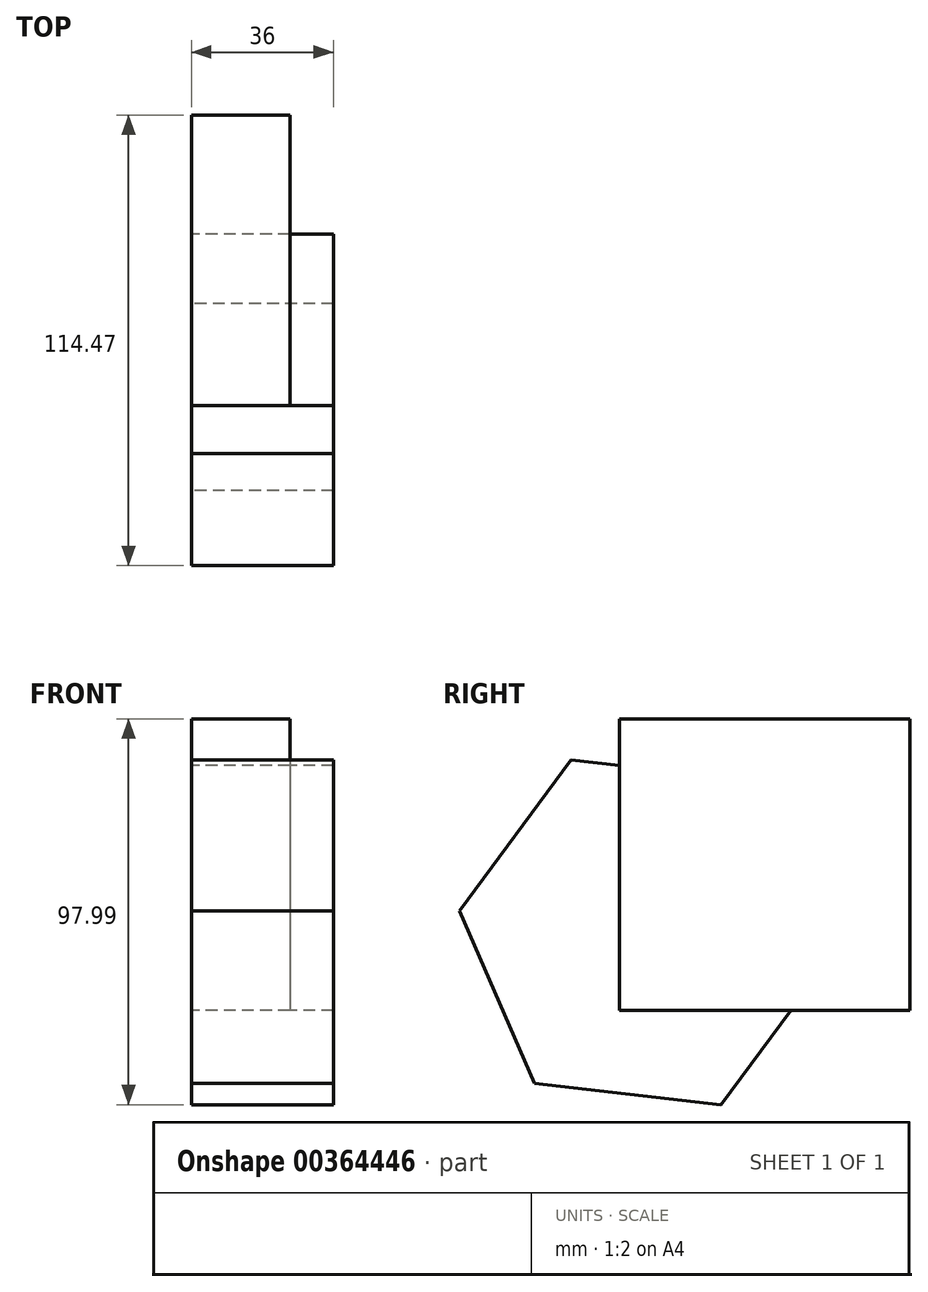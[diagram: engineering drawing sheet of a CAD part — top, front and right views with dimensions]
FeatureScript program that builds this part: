
annotation { "Feature Type Name" : "Feature", "Feature Type Description" : "" }
export const myFeature = defineFeature(function(context is Context, id is Id, definition is map)
    precondition{}
    {
        {
            var Q0;
            Q0=qCreatedBy(makeId("Right.planeOp"),FACE);
            var sketch = newSketch(context, id + "F0", { "sketchPlane" : qUnion([Q0])});
            skLineSegment(sketch, "E0.bottom", {"start": v(-50.7, 30.8) * mm, "end": v(23.12, 30.8) * mm});
            skLineSegment(sketch, "E0.top", {"start": v(-50.7, -43.25) * mm, "end": v(23.12, -43.25) * mm});
            skLineSegment(sketch, "E0.left", {"start": v(-50.7, 30.8) * mm, "end": v(-50.7, -43.25) * mm});
            skLineSegment(sketch, "E0.right", {"start": v(23.12, 30.8) * mm, "end": v(23.12, -43.25) * mm});
            skLineSegment(sketch, "E1.bottom", {"start": v(23.12, 30.8) * mm, "end": v(68.93, 30.8) * mm});
            skLineSegment(sketch, "E1.top", {"start": v(23.12, 0) * mm, "end": v(68.93, 0) * mm});
            skLineSegment(sketch, "E1.left", {"start": v(23.12, 30.8) * mm, "end": v(23.12, 0) * mm});
            skLineSegment(sketch, "E1.right", {"start": v(68.93, 30.8) * mm, "end": v(68.93, 0) * mm});
            skLineSegment(sketch, "E2.bottom", {"start": v(-103.5, -290.49) * mm, "end": v(-109.17, -290.49) * mm});
            skLineSegment(sketch, "E2.top", {"start": v(-103.5, -290.36) * mm, "end": v(-109.17, -290.36) * mm});
            skLineSegment(sketch, "E2.left", {"start": v(-103.5, -290.49) * mm, "end": v(-103.5, -290.36) * mm});
            skLineSegment(sketch, "E2.right", {"start": v(-109.17, -290.49) * mm, "end": v(-109.17, -290.36) * mm});
            skSolve(sketch);
        }
        {
            var Q0;
            Q0=makeQuery(id+"F0.imprint","IMPRINT",FACE,{"disambiguationData":[TD([[makeQuery(id+"F0.imprint","IMPRINT",EDGE,{"derivedFrom":sQuery(id+"F0.wireOp",EDGE,"E0.bottom")}),-1.0]])]});
            var sketch = newSketch(context, id + "F1", { "sketchPlane" : qUnion([Q0])});
            skCircle(sketch, "E3.cCircle", {"center": v(-43.88, -23.38) * mm, "radius": 47.78 * mm, "construction": true});
            skLineSegment(sketch, "E3.0", {"start": v(-91.35, -17.98) * mm, "end": v(-62.94, 20.43) * mm});
            skLineSegment(sketch, "E3.1", {"start": v(-62.94, 20.43) * mm, "end": v(-15.47, 15.03) * mm});
            skLineSegment(sketch, "E3.2", {"start": v(-15.47, 15.03) * mm, "end": v(3.6, -28.78) * mm});
            skLineSegment(sketch, "E3.3", {"start": v(3.6, -28.78) * mm, "end": v(-24.82, -67.19) * mm});
            skLineSegment(sketch, "E3.4", {"start": v(-24.82, -67.19) * mm, "end": v(-72.29, -61.8) * mm});
            skLineSegment(sketch, "E3.5", {"start": v(-72.29, -61.8) * mm, "end": v(-91.35, -17.98) * mm});
            skSolve(sketch);
        }
        {
            var Q0;
            Q0=qCreatedBy(makeId("Right.planeOp"),FACE);
            var sketch = newSketch(context, id + "F2", { "sketchPlane" : qUnion([Q0])});
            skLineSegment(sketch, "E4", {"start": v(23.12, 30.8) * mm, "end": v(23.12, 0) * mm});
            skLineSegment(sketch, "E5", {"start": v(-50.7, 30.8) * mm, "end": v(23.12, 30.8) * mm});
            skLineSegment(sketch, "E6", {"start": v(-50.7, 30.8) * mm, "end": v(-50.7, -43.25) * mm});
            skLineSegment(sketch, "E7", {"start": v(-50.7, -43.25) * mm, "end": v(23.12, -43.25) * mm});
            skLineSegment(sketch, "E8", {"start": v(23.12, 0) * mm, "end": v(23.12, -43.25) * mm});
            skLineSegment(sketch, "E9", {"start": v(-7.11, -43.25) * mm, "end": v(-24.82, -67.19) * mm});
            skLineSegment(sketch, "E10", {"start": v(-50.7, -43.25) * mm, "end": v(-7.11, -43.25) * mm});
            skLineSegment(sketch, "E11", {"start": v(-50.7, 19.04) * mm, "end": v(-50.7, -43.25) * mm});
            skLineSegment(sketch, "E12", {"start": v(-62.94, 20.43) * mm, "end": v(-50.7, 19.04) * mm});
            skLineSegment(sketch, "E13", {"start": v(-91.35, -17.98) * mm, "end": v(-62.94, 20.43) * mm});
            skLineSegment(sketch, "E14", {"start": v(-72.29, -61.8) * mm, "end": v(-91.35, -17.98) * mm});
            skLineSegment(sketch, "E15", {"start": v(-24.82, -67.19) * mm, "end": v(-72.29, -61.8) * mm});
            skSolve(sketch);
        }
        {
            var Q0;
            Q0=makeQuery(id+"F0.imprint","IMPRINT",FACE,{"disambiguationData":[TD([[makeQuery(id+"F0.imprint","IMPRINT",EDGE,{"derivedFrom":sQuery(id+"F0.wireOp",EDGE,"E0.bottom")}),-1.0]])]});
            var sketch = newSketch(context, id + "F3", { "sketchPlane" : qUnion([Q0])});
            skSolve(sketch);
        }
        {
            var Q0;
            Q0 = qSketchRegion(id + "F3", true);
            var Q1;
            Q1=makeQuery(id+"F2.imprint","IMPRINT",FACE,{"disambiguationData":[TD([[makeQuery(id+"F2.imprint","IMPRINT",EDGE,{"derivedFrom":sQuery(id+"F2.wireOp",EDGE,"E4")}),-1.0]])]});
            extrude(context, id + "F4", {"entities" : qUnion([Q0, Q1]), "depth" : 25 * mm});
        }
        {
            var Q0;
            {var subQ2=sQuery(id+"F1.wireOp",EDGE,"E3.0");Q0=makeQuery(id+"F1.imprint","IMPRINT",FACE,{"disambiguationData":[TD([[makeQuery(id+"F1.imprint","IMPRINT",EDGE,{"derivedFrom":subQ2}),-1.0]])]});}
            var sketch = newSketch(context, id + "F5", { "sketchPlane" : qUnion([Q0])});
            skSolve(sketch);
        }
        {
            var Q0;
            Q0 = qSketchRegion(id + "F5", true);
            var Q1;
            {var subQ2=sQuery(id+"F1.wireOp",EDGE,"E3.0");Q1=makeQuery(id+"F1.imprint","IMPRINT",FACE,{"disambiguationData":[TD([[makeQuery(id+"F1.imprint","IMPRINT",EDGE,{"derivedFrom":subQ2}),-1.0]])]});}
            extrude(context, id + "F6", {"entities" : qUnion([Q0, Q1]), "operationType" : NewBodyOperationType.ADD, "depth" : 36 * mm});
        }
    });
